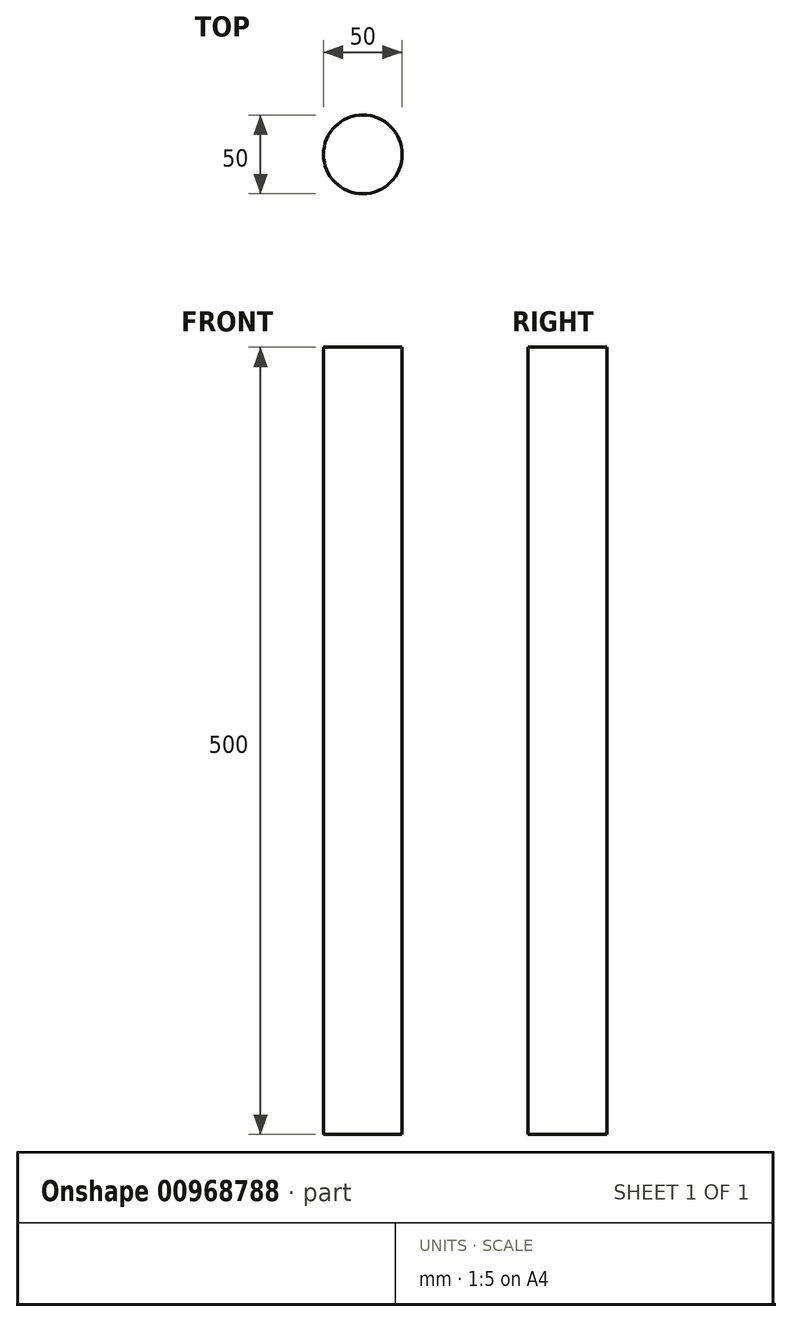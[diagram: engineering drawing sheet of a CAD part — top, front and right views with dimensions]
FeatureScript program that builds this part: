
annotation { "Feature Type Name" : "Feature", "Feature Type Description" : "" }
export const myFeature = defineFeature(function(context is Context, id is Id, definition is map)
    precondition{}
    {
        {
            var Q0;
            Q0=qCreatedBy(makeId("Top.planeOp"),FACE);
            var sketch = newSketch(context, id + "F0", { "sketchPlane" : qUnion([Q0])});
            skCircle(sketch, "E0", {"center": v(0, 0) * mm, "radius": 25 * mm});
            skSolve(sketch);
        }
        {
            var Q0;
            Q0 = qSketchRegion(id + "F0", true);
            extrude(context, id + "F1", {"entities" : qUnion([Q0]), "depth" : 500 * mm, "offsetDistance" : 25 * mm});
        }
    });
